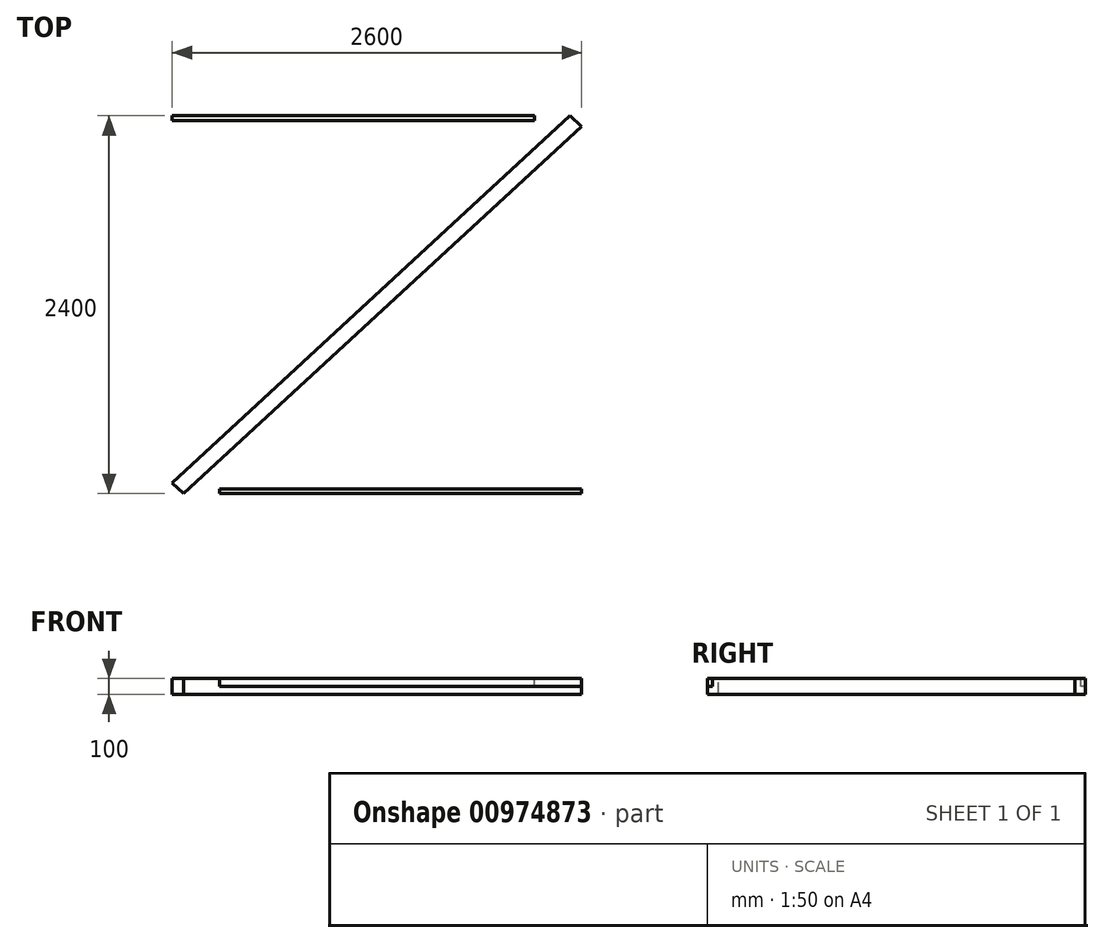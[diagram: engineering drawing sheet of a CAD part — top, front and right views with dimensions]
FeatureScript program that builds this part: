
annotation { "Feature Type Name" : "Feature", "Feature Type Description" : "" }
export const myFeature = defineFeature(function(context is Context, id is Id, definition is map)
    precondition{}
    {
        {
            var Q0;
            Q0=qCreatedBy(makeId("Top.planeOp"),FACE);
            var sketch = newSketch(context, id + "F0", { "sketchPlane" : qUnion([Q0])});
            skLineSegment(sketch, "E0.bottom", {"start": v(-650.8, 2969.05) * mm, "end": v(1949.2, 2969.05) * mm});
            skLineSegment(sketch, "E0.top", {"start": v(-650.8, 569.05) * mm, "end": v(1949.2, 569.05) * mm});
            skLineSegment(sketch, "E0.left", {"start": v(-650.8, 2969.05) * mm, "end": v(-650.8, 569.05) * mm});
            skLineSegment(sketch, "E0.right", {"start": v(1949.2, 2969.05) * mm, "end": v(1949.2, 569.05) * mm});
            skLineSegment(sketch, "E1", {"start": v(1912.33, 2935.03) * mm, "end": v(-613.95, 603.08) * mm});
            skLineSegment(sketch, "E2.0", {"start": v(1949.2, 2901) * mm, "end": v(-577.1, 569.05) * mm});
            skLineSegment(sketch, "E3.0", {"start": v(1875.48, 2969.05) * mm, "end": v(-650.8, 637.1) * mm});
            skLineSegment(sketch, "E4", {"start": v(1875.48, 2969.05) * mm, "end": v(1949.2, 2901) * mm});
            skLineSegment(sketch, "E5", {"start": v(-650.8, 637.1) * mm, "end": v(-577.1, 569.05) * mm});
            skLineSegment(sketch, "E6.bottom", {"start": v(-1150, 15) * mm, "end": v(1150, 15) * mm});
            skLineSegment(sketch, "E6.top", {"start": v(-1150, -15) * mm, "end": v(1150, -15) * mm});
            skLineSegment(sketch, "E6.left", {"start": v(-1150, 15) * mm, "end": v(-1150, -15) * mm});
            skLineSegment(sketch, "E6.right", {"start": v(1150, 15) * mm, "end": v(1150, -15) * mm});
            skSolve(sketch);
        }
        {
            var Q0;
            {var subQ0=sQuery(id+"F0.wireOp",EDGE,"E1");Q0=makeQuery(id+"F0.imprint","IMPRINT",FACE,{"disambiguationData":[TD([[makeQuery(id+"F0.imprint","IMPRINT",EDGE,{"derivedFrom":subQ0}),-1.0]])]});}
            var Q1;
            {var subQ0=sQuery(id+"F0.wireOp",EDGE,"E1");Q1=makeQuery(id+"F0.imprint","IMPRINT",FACE,{"disambiguationData":[TD([[makeQuery(id+"F0.imprint","IMPRINT",EDGE,{"derivedFrom":subQ0}),1.0]])]});}
            extrude(context, id + "F1", {"entities" : qUnion([Q0, Q1]), "oppositeDirection" : true, "depth" : 100 * mm, "offsetDistance" : 25 * mm});
        }
        {
            var Q0;
            Q0=qCreatedBy(makeId("Top.planeOp"),FACE);
            var sketch = newSketch(context, id + "F2", { "sketchPlane" : qUnion([Q0])});
            skLineSegment(sketch, "E7.bottom", {"start": v(-650.8, 2969.05) * mm, "end": v(1649.2, 2969.05) * mm});
            skLineSegment(sketch, "E7.top", {"start": v(-650.8, 2939.05) * mm, "end": v(1649.2, 2939.05) * mm});
            skLineSegment(sketch, "E7.left", {"start": v(-650.8, 2969.05) * mm, "end": v(-650.8, 2939.05) * mm});
            skLineSegment(sketch, "E7.right", {"start": v(1649.2, 2969.05) * mm, "end": v(1649.2, 2939.05) * mm});
            skLineSegment(sketch, "E8.bottom", {"start": v(1949.2, 569.05) * mm, "end": v(-350.8, 569.05) * mm});
            skLineSegment(sketch, "E8.top", {"start": v(1949.2, 599.05) * mm, "end": v(-350.8, 599.05) * mm});
            skLineSegment(sketch, "E8.left", {"start": v(1949.2, 569.05) * mm, "end": v(1949.2, 599.05) * mm});
            skLineSegment(sketch, "E8.right", {"start": v(-350.8, 569.05) * mm, "end": v(-350.8, 599.05) * mm});
            skSolve(sketch);
        }
        {
            var Q0;
            Q0=makeQuery(id+"F2.imprint","IMPRINT",FACE,{"disambiguationData":[TD([[makeQuery(id+"F2.imprint","IMPRINT",EDGE,{"derivedFrom":sQuery(id+"F2.wireOp",EDGE,"E7.bottom")}),-1.0]])]});
            extrude(context, id + "F3", {"entities" : qUnion([Q0]), "oppositeDirection" : true, "depth" : 50 * mm, "offsetDistance" : 25 * mm});
        }
        {
            var Q0;
            Q0=makeQuery(id+"F2.imprint","IMPRINT",FACE,{"disambiguationData":[TD([[makeQuery(id+"F2.imprint","IMPRINT",EDGE,{"derivedFrom":sQuery(id+"F2.wireOp",EDGE,"E8.bottom")}),-1.0]])]});
            extrude(context, id + "F4", {"entities" : qUnion([Q0]), "oppositeDirection" : true, "depth" : 50 * mm, "offsetDistance" : 25 * mm});
        }
    });
